# Revit family: Multidrawer 2
name_source: partatom
category: Furniture
revit_build: Autodesk Revit 2018 (Build: 20180423_1000(x64)
units: mm (PartAtom-declared; Revit-internal decimal feet)

## family parameters
Always vertical = No
Cut with Voids When Loaded = No
OmniClass Number = 23.40.20.00
OmniClass Title = General Furniture and Specialties
Room Calculation Point = No
Shared = No
Work Plane-Based = Yes

## types (11) — shared parameters
Category = Furniture
Compliance Standards Certification = BS EN 14073 2004 Part 2 & 3, BS EN 14074, BS 4875 1998 Part 7 level 4
Default Elevation = 1219 mm
Drawer 1 = Yes
Drawer 2 = Yes
Drawer 3 = Yes
Expected Life = 5-10 years
Finish = Powder Coated
Manufacturer = Bisley
Material = Steel
Range = Multidrawer
Routine Maintenance = We recommend you clean your unit with warm water and a mild detergent solution. A damp cloth can be used to remove dust particles.
URL = www.bisley.com
Uniclass 2015 Code = PR-40-30-25
Uniclass2015Title = Shelves and Storage Units
Uniclass2015Version = V1.1
Warranty = 5 Years

## per-type parameters (varying)
- H123NL: Base=No; Depth=380 mm; Description=3 Drawer A4 Unit; Dimensions=325 x 279 x 380 mm; Drawer 10=No; Drawer 11=No; Drawer 12=No; Drawer 13=No; Drawer 14=No; Drawer 15=No; Drawer 4=No; Drawer 5=No; Drawer 6=No; Drawer 7=No; Drawer 8=No; Drawer 9=No; Drawer Height=87 mm  [stored 0.285433 ft]; Drawer Type=51mm drawer : 87mm; Drawer Type 1=51mm drawer : 87mm; Drawer Type 2=51mm drawer : 87mm; Drawer Type 3=51mm drawer : 87mm; Drawer Type 4=51mm drawer : 87mm; Drawer Type 5=51mm drawer : 87mm; Drawer Type 6=51mm drawer : 87mm; Drawer Type 7=51mm drawer : 87mm; Drawer Type 8=51mm drawer : 87mm; Height=325 mm  [stored 1.06627 ft]; Height 1=87 mm  [stored 0.285433 ft]; Height 2=87 mm  [stored 0.285433 ft]; Height 3=87 mm  [stored 0.285433 ft]; Height 4=87 mm  [stored 0.285433 ft]; Height 5=87 mm  [stored 0.285433 ft]; Height 6=87 mm  [stored 0.285433 ft]; Height 7=87 mm  [stored 0.285433 ft]; Height 8=87 mm  [stored 0.285433 ft]; Product Information=3 Drawer A4 Unit; Tolerance=2 mm  [stored 0.00656168 ft]; Tollerance 2=1 mm  [stored 0.00328084 ft]; Weight=7.1kg; Width=273 mm; drawer mid point=44 mm
- H125NL: Base=No; Depth=380 mm; Description=5 Drawer A4 Unit; Dimensions=325 x 279 x 380 mm; Drawer 10=No; Drawer 11=No; Drawer 12=No; Drawer 13=No; Drawer 14=No; Drawer 15=No; Drawer 4=Yes; Drawer 5=Yes; Drawer 6=No; Drawer 7=No; Drawer 8=No; Drawer 9=No; Drawer Height=51 mm; Drawer Type=51mm drawer : 51mm; Drawer Type 1=51mm drawer : 51mm; Drawer Type 2=51mm drawer : 51mm; Drawer Type 3=51mm drawer : 51mm; Drawer Type 4=51mm drawer : 51mm; Drawer Type 5=51mm drawer : 51mm; Drawer Type 6=51mm drawer : 51mm; Drawer Type 7=51mm drawer : 51mm; Drawer Type 8=51mm drawer : 51mm; Height=325 mm  [stored 1.06627 ft]; Height 1=51 mm; Height 2=51 mm; Height 3=51 mm; Height 4=51 mm; Height 5=51 mm; Height 6=51 mm; Height 7=51 mm; Height 8=51 mm; Product Information=5 Drawer A4 Unit; Tolerance=1 mm  [stored 0.00328084 ft]; Tollerance 2=2 mm  [stored 0.00656168 ft]; Weight=9.18kg; Width=279 mm; drawer mid point=26 mm
- H298BNL: Base=No; Depth=380 mm; Description=8 Drawer A4 Unit; Dimensions=590 x 279 x 380 mm; Drawer 10=No; Drawer 11=No; Drawer 12=No; Drawer 13=No; Drawer 14=No; Drawer 15=No; Drawer 4=Yes; Drawer 5=Yes; Drawer 6=Yes; Drawer 7=Yes; Drawer 8=Yes; Drawer 9=No; Drawer Height=51 mm; Drawer Type=51mm drawer : 51mm; Drawer Type 1=51mm drawer : 102mm; Drawer Type 2=51mm drawer : 102mm; Drawer Type 3=51mm drawer : 102mm; Drawer Type 4=51mm drawer : 51mm; Drawer Type 5=51mm drawer : 51mm; Drawer Type 6=51mm drawer : 51mm; Drawer Type 7=51mm drawer : 25mm; Drawer Type 8=51mm drawer : 25mm; Height=590 mm  [stored 1.9357 ft]; Height 1=102 mm; Height 2=102 mm; Height 3=102 mm; Height 4=51 mm; Height 5=51 mm; Height 6=51 mm; Height 7=25 mm  [stored 0.082021 ft]; Height 8=25 mm  [stored 0.082021 ft]; Product Information=8 Drawer A4 Unit; Tolerance=1 mm  [stored 0.00328084 ft]; Tollerance 2=2 mm  [stored 0.00656168 ft]; Weight=14.46kg; Width=279 mm; drawer mid point=26 mm
- H296NL: Base=No; Depth=380 mm; Description=6 Drawer A4 Unit; Dimensions=590 x 279 x 380 mm; Drawer 10=No; Drawer 11=No; Drawer 12=No; Drawer 13=No; Drawer 14=No; Drawer 15=No; Drawer 4=Yes; Drawer 5=Yes; Drawer 6=Yes; Drawer 7=No; Drawer 8=No; Drawer 9=No; Drawer Height=87 mm  [stored 0.285433 ft]; Drawer Type=51mm drawer : 51mm; Drawer Type 1=51mm drawer : 87mm; Drawer Type 2=51mm drawer : 87mm; Drawer Type 3=51mm drawer : 87mm; Drawer Type 4=51mm drawer : 87mm; Drawer Type 5=51mm drawer : 87mm; Drawer Type 6=51mm drawer : 87mm; Drawer Type 7=51mm drawer : 87mm; Drawer Type 8=51mm drawer : 87mm; Height=590 mm  [stored 1.9357 ft]; Height 1=87 mm  [stored 0.285433 ft]; Height 2=87 mm  [stored 0.285433 ft]; Height 3=87 mm  [stored 0.285433 ft]; Height 4=87 mm  [stored 0.285433 ft]; Height 5=87 mm  [stored 0.285433 ft]; Height 6=87 mm  [stored 0.285433 ft]; Height 7=87 mm  [stored 0.285433 ft]; Height 8=87 mm  [stored 0.285433 ft]; Product Information=6 Drawer A4 Unit; Tolerance=1 mm  [stored 0.00328084 ft]; Tollerance 2=1 mm  [stored 0.00328084 ft]; Weight=13.21kg; Width=279 mm; drawer mid point=44 mm
- H2910NL: Base=No; Depth=380 mm; Description=10 Drawer A4 Unit; Dimensions=590 x 279 x 380 mm; Drawer 10=Yes; Drawer 11=No; Drawer 12=No; Drawer 13=No; Drawer 14=No; Drawer 15=No; Drawer 4=Yes; Drawer 5=Yes; Drawer 6=Yes; Drawer 7=Yes; Drawer 8=Yes; Drawer 9=Yes; Drawer Height=51 mm; Drawer Type=51mm drawer : 51mm; Drawer Type 1=51mm drawer : 51mm; Drawer Type 2=51mm drawer : 51mm; Drawer Type 3=51mm drawer : 51mm; Drawer Type 4=51mm drawer : 51mm; Drawer Type 5=51mm drawer : 51mm; Drawer Type 6=51mm drawer : 51mm; Drawer Type 7=51mm drawer : 51mm; Drawer Type 8=51mm drawer : 51mm; Height=590 mm  [stored 1.9357 ft]; Height 1=51 mm; Height 2=51 mm; Height 3=51 mm; Height 4=51 mm; Height 5=51 mm; Height 6=51 mm; Height 7=51 mm; Height 8=51 mm; Product Information=10 Drawer A4 Unit; Tolerance=1 mm  [stored 0.00328084 ft]; Tollerance 2=2 mm  [stored 0.00656168 ft]; Weight=15.25kg; Width=279 mm; drawer mid point=26 mm
- H399NL: Base=No; Depth=380 mm; Description=9 Drawer A4 Unit; Dimensions=860 x 279 x 380 mm; Drawer 10=No; Drawer 11=No; Drawer 12=No; Drawer 13=No; Drawer 14=No; Drawer 15=No; Drawer 4=Yes; Drawer 5=Yes; Drawer 6=Yes; Drawer 7=Yes; Drawer 8=Yes; Drawer 9=Yes; Drawer Height=87 mm  [stored 0.285433 ft]; Drawer Type=51mm drawer : 87mm; Drawer Type 1=51mm drawer : 87mm; Drawer Type 2=51mm drawer : 87mm; Drawer Type 3=51mm drawer : 87mm; Drawer Type 4=51mm drawer : 87mm; Drawer Type 5=51mm drawer : 87mm; Drawer Type 6=51mm drawer : 87mm; Drawer Type 7=51mm drawer : 87mm; Drawer Type 8=51mm drawer : 87mm; Height=860 mm  [stored 2.82152 ft]; Height 1=87 mm  [stored 0.285433 ft]; Height 2=87 mm  [stored 0.285433 ft]; Height 3=87 mm  [stored 0.285433 ft]; Height 4=87 mm  [stored 0.285433 ft]; Height 5=87 mm  [stored 0.285433 ft]; Height 6=87 mm  [stored 0.285433 ft]; Height 7=87 mm  [stored 0.285433 ft]; Height 8=87 mm  [stored 0.285433 ft]; Product Information=9 Drawer A4 Unit; Tolerance=1 mm  [stored 0.00328084 ft]; Tollerance 2=2 mm  [stored 0.00656168 ft]; Weight=18.2kg; Width=279 mm; drawer mid point=44 mm
- H3915NL: Base=No; Depth=380 mm; Description=15 Drawer A4 Unit; Dimensions=860 x 279 x 380 mm; Drawer 10=Yes; Drawer 11=Yes; Drawer 12=Yes; Drawer 13=Yes; Drawer 14=Yes; Drawer 15=Yes; Drawer 4=Yes; Drawer 5=Yes; Drawer 6=Yes; Drawer 7=Yes; Drawer 8=Yes; Drawer 9=Yes; Drawer Height=51 mm; Drawer Type=51mm drawer : 51mm; Drawer Type 1=51mm drawer : 51mm; Drawer Type 2=51mm drawer : 51mm; Drawer Type 3=51mm drawer : 51mm; Drawer Type 4=51mm drawer : 51mm; Drawer Type 5=51mm drawer : 51mm; Drawer Type 6=51mm drawer : 51mm; Drawer Type 7=51mm drawer : 51mm; Drawer Type 8=51mm drawer : 51mm; Height=860 mm  [stored 2.82152 ft]; Height 1=52 mm; Height 2=51 mm; Height 3=51 mm; Height 4=51 mm; Height 5=51 mm; Height 6=51 mm; Height 7=51 mm; Height 8=51 mm; Product Information=15 Drawer A4 Unit; Tolerance=1 mm  [stored 0.00328084 ft]; Tollerance 2=2 mm  [stored 0.00656168 ft]; Weight=21.32kg; Width=279 mm; drawer mid point=26 mm
- 112: Base=Yes; Depth=432 mm  [stored 1.41732 ft]; Description=6 Drawer A3 Unit; Dimensions=670 x 349 x 432 mm; Drawer 10=No; Drawer 11=No; Drawer 12=No; Drawer 13=No; Drawer 14=No; Drawer 15=No; Drawer 4=Yes; Drawer 5=Yes; Drawer 6=Yes; Drawer 7=No; Drawer 8=No; Drawer 9=No; Drawer Height=87 mm  [stored 0.285433 ft]; Drawer Type=51mm drawer : 87mm; Drawer Type 1=51mm drawer : A3 87mm; Drawer Type 2=51mm drawer : A3 87mm; Drawer Type 3=51mm drawer : A3 87mm; Drawer Type 4=51mm drawer : A3 87mm; Drawer Type 5=51mm drawer : A3 87mm; Drawer Type 6=51mm drawer : A3 87mm; Drawer Type 7=51mm drawer : A3 87mm; Drawer Type 8=51mm drawer : A3 87mm; Height=590 mm  [stored 1.9357 ft]; Height 1=87 mm  [stored 0.285433 ft]; Height 2=87 mm  [stored 0.285433 ft]; Height 3=87 mm  [stored 0.285433 ft]; Height 4=87 mm  [stored 0.285433 ft]; Height 5=87 mm  [stored 0.285433 ft]; Height 6=87 mm  [stored 0.285433 ft]; Height 7=87 mm  [stored 0.285433 ft]; Height 8=87 mm  [stored 0.285433 ft]; Product Information=6 Drawer A3 Unit; Tolerance=1 mm  [stored 0.00328084 ft]; Tollerance 2=1 mm  [stored 0.00328084 ft]; Weight=18.04kg; Width=349 mm  [stored 1.14501 ft]; drawer mid point=44 mm
- 116: Base=Yes; Depth=432 mm  [stored 1.41732 ft]; Description=10 Drawer A3 unit; Dimensions=670 x 349 x 432; Drawer 10=Yes; Drawer 11=No; Drawer 12=No; Drawer 13=No; Drawer 14=No; Drawer 15=No; Drawer 4=Yes; Drawer 5=Yes; Drawer 6=Yes; Drawer 7=Yes; Drawer 8=Yes; Drawer 9=Yes; Drawer Height=51 mm; Drawer Type=51mm drawer : A3 51mm; Drawer Type 1=51mm drawer : A3 51mm; Drawer Type 2=51mm drawer : A3 51mm; Drawer Type 3=51mm drawer : A3 51mm; Drawer Type 4=51mm drawer : A3 51mm; Drawer Type 5=51mm drawer : A3 51mm; Drawer Type 6=51mm drawer : A3 51mm; Drawer Type 7=51mm drawer : A3 51mm; Drawer Type 8=51mm drawer : A3 51mm; Height=590 mm  [stored 1.9357 ft]; Height 1=51 mm; Height 2=51 mm; Height 3=51 mm; Height 4=51 mm; Height 5=51 mm; Height 6=51 mm; Height 7=51 mm; Height 8=51 mm; Product Information=10 Drawer A3 unit; Tolerance=1 mm  [stored 0.00328084 ft]; Tollerance 2=2 mm  [stored 0.00656168 ft]; Weight=21.43kg; Width=349 mm  [stored 1.14501 ft]; drawer mid point=26 mm
- 114: Base=Yes; Depth=432 mm  [stored 1.41732 ft]; Description=9 Drawer A3 Unit; Dimensions=940 x 349 x 432 mm; Drawer 10=No; Drawer 11=No; Drawer 12=No; Drawer 13=No; Drawer 14=No; Drawer 15=No; Drawer 4=Yes; Drawer 5=Yes; Drawer 6=Yes; Drawer 7=Yes; Drawer 8=Yes; Drawer 9=Yes; Drawer Height=87 mm  [stored 0.285433 ft]; Drawer Type=51mm drawer : A3 87mm; Drawer Type 1=51mm drawer : A3 87mm; Drawer Type 2=51mm drawer : A3 87mm; Drawer Type 3=51mm drawer : A3 87mm; Drawer Type 4=51mm drawer : A3 87mm; Drawer Type 5=51mm drawer : A3 87mm; Drawer Type 6=51mm drawer : A3 87mm; Drawer Type 7=51mm drawer : A3 87mm; Drawer Type 8=51mm drawer : A3 87mm; Height=860 mm  [stored 2.82152 ft]; Height 1=87 mm  [stored 0.285433 ft]; Height 2=87 mm  [stored 0.285433 ft]; Height 3=87 mm  [stored 0.285433 ft]; Height 4=87 mm  [stored 0.285433 ft]; Height 5=87 mm  [stored 0.285433 ft]; Height 6=87 mm  [stored 0.285433 ft]; Height 7=87 mm  [stored 0.285433 ft]; Height 8=87 mm  [stored 0.285433 ft]; Product Information=9 Drawer A3 Unit; Tolerance=1 mm  [stored 0.00328084 ft]; Tollerance 2=2 mm  [stored 0.00656168 ft]; Weight=24.37kg; Width=349 mm  [stored 1.14501 ft]; drawer mid point=44 mm
- 118: Base=Yes; Depth=432 mm  [stored 1.41732 ft]; Description=15 Drawer A3 Unit; Dimensions=940 x 349 x 432 mm; Drawer 10=Yes; Drawer 11=Yes; Drawer 12=Yes; Drawer 13=Yes; Drawer 14=Yes; Drawer 15=Yes; Drawer 4=Yes; Drawer 5=Yes; Drawer 6=Yes; Drawer 7=Yes; Drawer 8=Yes; Drawer 9=Yes; Drawer Height=51 mm; Drawer Type=51mm drawer : A3 51mm; Drawer Type 1=51mm drawer : A3 51mm; Drawer Type 2=51mm drawer : A3 51mm; Drawer Type 3=51mm drawer : A3 51mm; Drawer Type 4=51mm drawer : A3 51mm; Drawer Type 5=51mm drawer : A3 51mm; Drawer Type 6=51mm drawer : A3 51mm; Drawer Type 7=51mm drawer : A3 51mm; Drawer Type 8=51mm drawer : A3 51mm; Height=860 mm  [stored 2.82152 ft]; Height 1=51 mm; Height 2=51 mm; Height 3=51 mm; Height 4=51 mm; Height 5=51 mm; Height 6=51 mm; Height 7=51 mm; Height 8=51 mm; Product Information=15 Drawer A3 Unit; Tolerance=1 mm  [stored 0.00328084 ft]; Tollerance 2=2 mm  [stored 0.00656168 ft]; Weight=28.89kg; Width=349 mm  [stored 1.14501 ft]; drawer mid point=26 mm

note: column(s) folded — value = type name in every type: Model Reference

note: [stored X ft] marks values corroborated as IEEE doubles in the binary element streams (Revit-internal decimal feet)

## geometry (parser evidence)
native form markers: Sweep x12
no freeform markers — native parametric forms only
